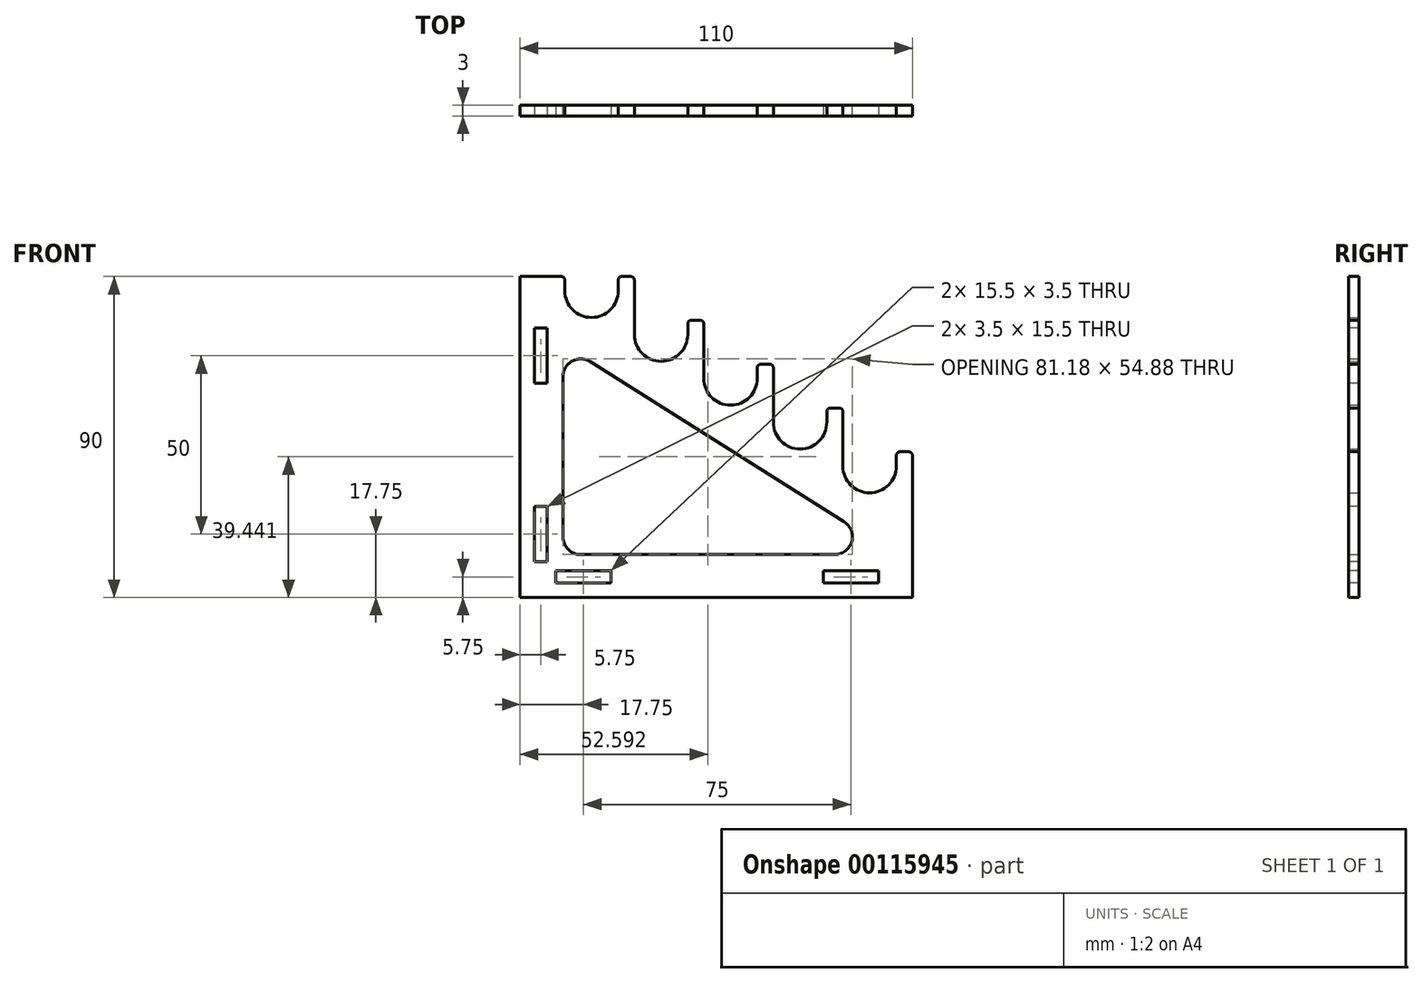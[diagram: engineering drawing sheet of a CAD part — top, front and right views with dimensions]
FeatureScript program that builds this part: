
annotation { "Feature Type Name" : "Feature", "Feature Type Description" : "" }
export const myFeature = defineFeature(function(context is Context, id is Id, definition is map)
    precondition{}
    {
        {
            var Q0;
            Q0=qCreatedBy(makeId("Front.planeOp"),FACE);
            var sketch = newSketch(context, id + "F0", { "sketchPlane" : qUnion([Q0]), "disableImprinting" : false});
            skLineSegment(sketch, "E0", {"start": v(0, 0) * mm, "end": v(110, 0) * mm});
            skLineSegment(sketch, "E1", {"start": v(0, 0) * mm, "end": v(0, 90) * mm});
            skLineSegment(sketch, "E2", {"start": v(13.66, 90) * mm, "end": v(110, 29.26) * mm, "construction": true});
            skArc(sketch, "E3", {"start": v(12.5, 86) * mm, "mid": v(20, 78.5) * mm, "end": v(27.5, 86) * mm});
            skArc(sketch, "E4", {"start": v(32, 73.7) * mm, "mid": v(39.5, 66.2) * mm, "end": v(47, 73.7) * mm});
            skArc(sketch, "E5", {"start": v(51.5, 61.41) * mm, "mid": v(59, 53.91) * mm, "end": v(66.5, 61.41) * mm});
            skArc(sketch, "E6", {"start": v(71, 49.12) * mm, "mid": v(78.5, 41.62) * mm, "end": v(86, 49.12) * mm});
            skArc(sketch, "E7", {"start": v(90.5, 36.82) * mm, "mid": v(98, 29.32) * mm, "end": v(105.5, 36.82) * mm});
            skLineSegment(sketch, "E8", {"start": v(27.5, 90) * mm, "end": v(32, 90) * mm});
            skLineSegment(sketch, "E9", {"start": v(32, 90) * mm, "end": v(32, 73.7) * mm});
            skLineSegment(sketch, "E10", {"start": v(47, 77.7) * mm, "end": v(51.5, 77.7) * mm});
            skLineSegment(sketch, "E11", {"start": v(51.5, 77.7) * mm, "end": v(51.5, 61.41) * mm});
            skLineSegment(sketch, "E12", {"start": v(71, 65.41) * mm, "end": v(71, 49.12) * mm});
            skLineSegment(sketch, "E13", {"start": v(86, 53.12) * mm, "end": v(90.5, 53.12) * mm});
            skLineSegment(sketch, "E14", {"start": v(90.5, 53.12) * mm, "end": v(90.5, 36.82) * mm});
            skLineSegment(sketch, "E15", {"start": v(110, 40.82) * mm, "end": v(110, 0) * mm});
            skLineSegment(sketch, "E16", {"start": v(12.5, 90) * mm, "end": v(0, 90) * mm});
            skLineSegment(sketch, "E17", {"start": v(12.5, 86) * mm, "end": v(12.5, 90) * mm});
            skLineSegment(sketch, "E18", {"start": v(27.5, 86) * mm, "end": v(27.5, 90) * mm});
            skLineSegment(sketch, "E19", {"start": v(47, 73.7) * mm, "end": v(47, 77.7) * mm});
            skLineSegment(sketch, "E20", {"start": v(66.5, 61.41) * mm, "end": v(66.5, 65.41) * mm});
            skLineSegment(sketch, "E21", {"start": v(86, 49.12) * mm, "end": v(86, 53.12) * mm});
            skLineSegment(sketch, "E22", {"start": v(105.5, 36.82) * mm, "end": v(105.5, 40.82) * mm});
            skLineSegment(sketch, "E23.trimOffspring", {"start": v(66.5, 65.41) * mm, "end": v(71, 65.41) * mm});
            skLineSegment(sketch, "E24.trimOffspring", {"start": v(105.5, 40.82) * mm, "end": v(110, 40.82) * mm});
            skPoint(sketch, "E25.orphan", {"position": v(91.66, 40.82) * mm});
            skLineSegment(sketch, "E26.0", {"start": v(12, 17) * mm, "end": v(12, 61.88) * mm});
            skLineSegment(sketch, "E27.0", {"start": v(17, 12) * mm, "end": v(88.19, 12) * mm});
            skLineSegment(sketch, "E28.0", {"start": v(19.67, 66.11) * mm, "end": v(90.86, 21.23) * mm});
            skArc(sketch, "E29.filletArc", {"start": v(19.67, 66.11) * mm, "mid": v(14.58, 66.26) * mm, "end": v(12, 61.88) * mm});
            skArc(sketch, "E30.filletArc", {"start": v(12, 17) * mm, "mid": v(13.46, 13.46) * mm, "end": v(17, 12) * mm});
            skArc(sketch, "E31.filletArc", {"start": v(88.19, 12) * mm, "mid": v(93, 15.61) * mm, "end": v(90.86, 21.23) * mm});
            skSolve(sketch);
        }
        {
            var Q0;
            Q0 = qSketchRegion(id + "F0", true);
            extrude(context, id + "F1", {"entities" : qUnion([Q0]), "depth" : 3 * mm});
        }
        {
            var Q0;
            Q0=makeQuery(id+"F1.opExtrude","SWEPT_EDGE",EDGE,{"disambiguationData":[OSD([sQuery(id+"F0.wireOp",EDGE,"E16"),sQuery(id+"F0.wireOp",EDGE,"E17")])]});
            var Q1;
            Q1=makeQuery(id+"F1.opExtrude","SWEPT_EDGE",EDGE,{"disambiguationData":[OSD([sQuery(id+"F0.wireOp",EDGE,"E8"),sQuery(id+"F0.wireOp",EDGE,"E18")])]});
            var Q2;
            Q2=makeQuery(id+"F1.opExtrude","SWEPT_EDGE",EDGE,{"disambiguationData":[OSD([sQuery(id+"F0.wireOp",EDGE,"E8"),sQuery(id+"F0.wireOp",EDGE,"E9")])]});
            var Q3;
            Q3=makeQuery(id+"F1.opExtrude","SWEPT_EDGE",EDGE,{"disambiguationData":[OSD([sQuery(id+"F0.wireOp",EDGE,"E10"),sQuery(id+"F0.wireOp",EDGE,"E19")])]});
            var Q4;
            Q4=makeQuery(id+"F1.opExtrude","SWEPT_EDGE",EDGE,{"disambiguationData":[OSD([sQuery(id+"F0.wireOp",EDGE,"E10"),sQuery(id+"F0.wireOp",EDGE,"E11")])]});
            var Q5;
            Q5=makeQuery(id+"F1.opExtrude","SWEPT_EDGE",EDGE,{"disambiguationData":[OSD([sQuery(id+"F0.wireOp",EDGE,"E20"),sQuery(id+"F0.wireOp",EDGE,"E23.trimOffspring")])]});
            var Q6;
            Q6=makeQuery(id+"F1.opExtrude","SWEPT_EDGE",EDGE,{"disambiguationData":[OSD([sQuery(id+"F0.wireOp",EDGE,"E12"),sQuery(id+"F0.wireOp",EDGE,"E23.trimOffspring")])]});
            var Q7;
            Q7=makeQuery(id+"F1.opExtrude","SWEPT_EDGE",EDGE,{"disambiguationData":[OSD([sQuery(id+"F0.wireOp",EDGE,"E15"),sQuery(id+"F0.wireOp",EDGE,"E24.trimOffspring")])]});
            var Q8;
            Q8=makeQuery(id+"F1.opExtrude","SWEPT_EDGE",EDGE,{"disambiguationData":[OSD([sQuery(id+"F0.wireOp",EDGE,"E22"),sQuery(id+"F0.wireOp",EDGE,"E24.trimOffspring")])]});
            var Q9;
            Q9=makeQuery(id+"F1.opExtrude","SWEPT_EDGE",EDGE,{"disambiguationData":[OSD([sQuery(id+"F0.wireOp",EDGE,"E13"),sQuery(id+"F0.wireOp",EDGE,"E14")])]});
            var Q10;
            Q10=makeQuery(id+"F1.opExtrude","SWEPT_EDGE",EDGE,{"disambiguationData":[OSD([sQuery(id+"F0.wireOp",EDGE,"E13"),sQuery(id+"F0.wireOp",EDGE,"E21")])]});
            fillet(context, id + "F2", {"entities" : qUnion([Q0, Q1, Q2, Q3, Q4, Q5, Q6, Q7, Q8, Q9, Q10]), "radius" : 1 * mm, "tangentPropagation" : true, "allowEdgeOverflow" : false});
        }
        {
            var Q0;
            Q0=makeQuery(id+"F1.opExtrude","CAP_FACE",FACE,{"disambiguationData":[OSD([sQuery(id+"F0.wireOp",EDGE,"E0"),sQuery(id+"F0.wireOp",EDGE,"E1"),sQuery(id+"F0.wireOp",EDGE,"E3"),sQuery(id+"F0.wireOp",EDGE,"E4"),sQuery(id+"F0.wireOp",EDGE,"E5"),sQuery(id+"F0.wireOp",EDGE,"E6"),sQuery(id+"F0.wireOp",EDGE,"E7"),sQuery(id+"F0.wireOp",EDGE,"E8"),sQuery(id+"F0.wireOp",EDGE,"E9"),sQuery(id+"F0.wireOp",EDGE,"E10"),sQuery(id+"F0.wireOp",EDGE,"E11"),sQuery(id+"F0.wireOp",EDGE,"E12"),sQuery(id+"F0.wireOp",EDGE,"E13"),sQuery(id+"F0.wireOp",EDGE,"E14"),sQuery(id+"F0.wireOp",EDGE,"E15"),sQuery(id+"F0.wireOp",EDGE,"E16"),sQuery(id+"F0.wireOp",EDGE,"E17"),sQuery(id+"F0.wireOp",EDGE,"E18"),sQuery(id+"F0.wireOp",EDGE,"E19"),sQuery(id+"F0.wireOp",EDGE,"E20"),sQuery(id+"F0.wireOp",EDGE,"E21"),sQuery(id+"F0.wireOp",EDGE,"E22"),sQuery(id+"F0.wireOp",EDGE,"E23.trimOffspring"),sQuery(id+"F0.wireOp",EDGE,"E24.trimOffspring"),sQuery(id+"F0.wireOp",EDGE,"E26.0"),sQuery(id+"F0.wireOp",EDGE,"E27.0"),sQuery(id+"F0.wireOp",EDGE,"E28.0"),sQuery(id+"F0.wireOp",EDGE,"E29.filletArc"),sQuery(id+"F0.wireOp",EDGE,"E30.filletArc"),sQuery(id+"F0.wireOp",EDGE,"E31.filletArc")])],"isStart":false});
            var sketch = newSketch(context, id + "F3", { "sketchPlane" : qUnion([Q0])});
            skLineSegment(sketch, "E32.bottom", {"start": v(10, 7.5) * mm, "end": v(25.5, 7.5) * mm});
            skLineSegment(sketch, "E32.top", {"start": v(10, 4) * mm, "end": v(25.5, 4) * mm});
            skLineSegment(sketch, "E32.left", {"start": v(10, 7.5) * mm, "end": v(10, 4) * mm});
            skLineSegment(sketch, "E32.right", {"start": v(25.5, 7.5) * mm, "end": v(25.5, 4) * mm});
            skLineSegment(sketch, "E33.bottom", {"start": v(85, 7.5) * mm, "end": v(100.5, 7.5) * mm});
            skLineSegment(sketch, "E33.top", {"start": v(85, 4) * mm, "end": v(100.5, 4) * mm});
            skLineSegment(sketch, "E33.left", {"start": v(85, 7.5) * mm, "end": v(85, 4) * mm});
            skLineSegment(sketch, "E33.right", {"start": v(100.5, 7.5) * mm, "end": v(100.5, 4) * mm});
            skLineSegment(sketch, "E34.bottom", {"start": v(4, 25.5) * mm, "end": v(7.5, 25.5) * mm});
            skLineSegment(sketch, "E34.top", {"start": v(4, 10) * mm, "end": v(7.5, 10) * mm});
            skLineSegment(sketch, "E34.left", {"start": v(4, 25.5) * mm, "end": v(4, 10) * mm});
            skLineSegment(sketch, "E34.right", {"start": v(7.5, 25.5) * mm, "end": v(7.5, 10) * mm});
            skLineSegment(sketch, "E35.bottom", {"start": v(4, 75.5) * mm, "end": v(7.5, 75.5) * mm});
            skLineSegment(sketch, "E35.top", {"start": v(4, 60) * mm, "end": v(7.5, 60) * mm});
            skLineSegment(sketch, "E35.left", {"start": v(4, 75.5) * mm, "end": v(4, 60) * mm});
            skLineSegment(sketch, "E35.right", {"start": v(7.5, 75.5) * mm, "end": v(7.5, 60) * mm});
            skSolve(sketch);
        }
        {
            var Q0;
            Q0 = qSketchRegion(id + "F3", true);
            extrude(context, id + "F4", {"entities" : qUnion([Q0]), "operationType" : NewBodyOperationType.REMOVE, "oppositeDirection" : true, "depth" : 25 * mm});
        }
    });
